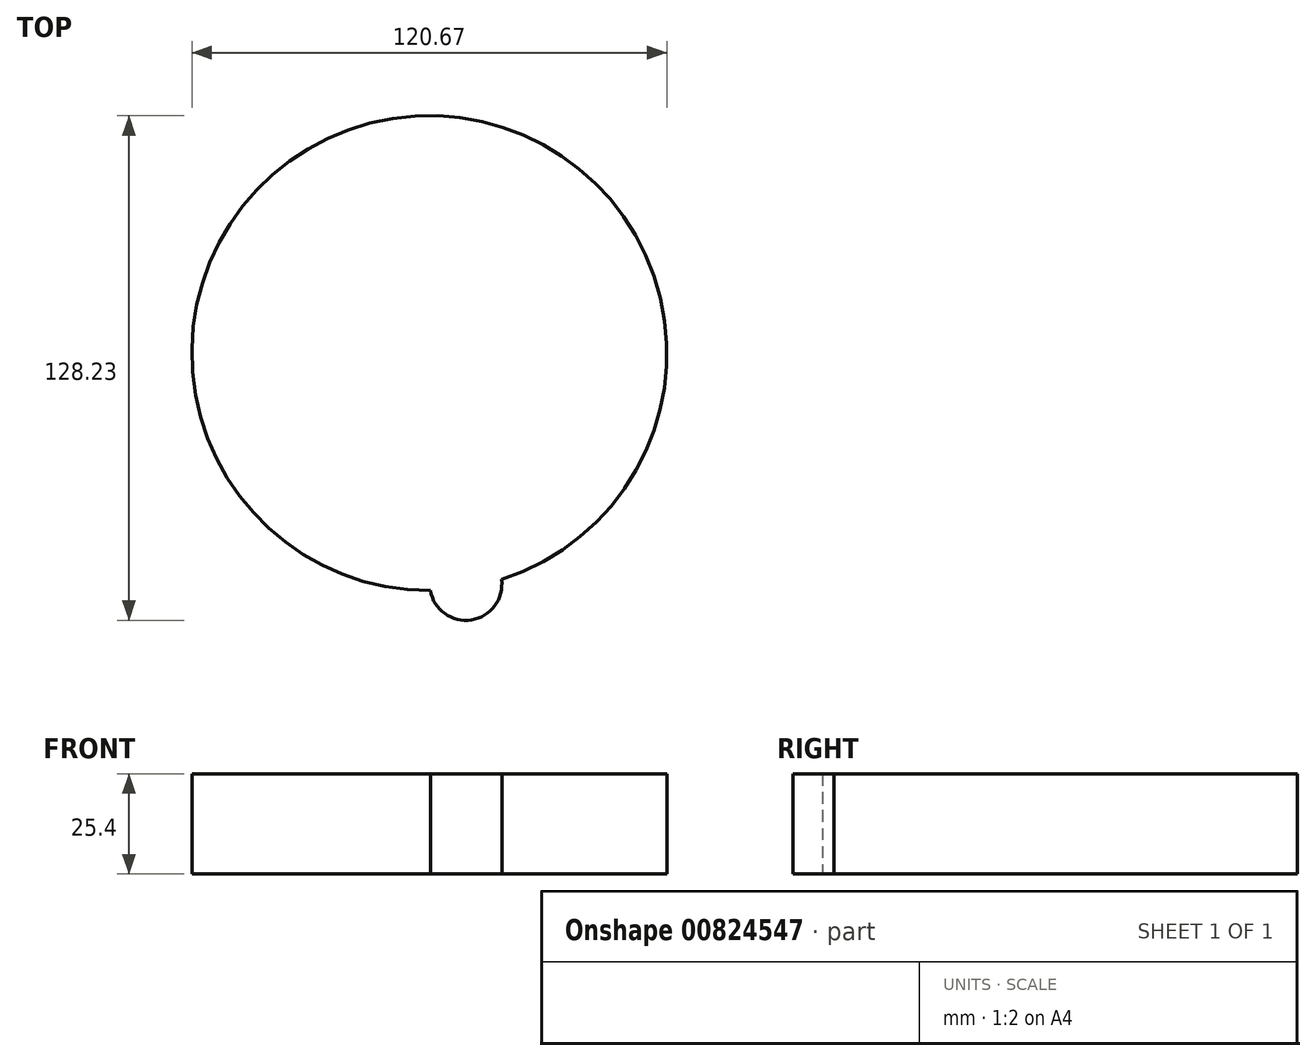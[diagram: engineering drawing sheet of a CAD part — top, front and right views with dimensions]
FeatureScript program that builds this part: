
annotation { "Feature Type Name" : "Feature", "Feature Type Description" : "" }
export const myFeature = defineFeature(function(context is Context, id is Id, definition is map)
    precondition{}
    {
        {
            var Q0;
            Q0=qCreatedBy(makeId("Top.planeOp"),FACE);
            var sketch = newSketch(context, id + "F0", { "sketchPlane" : qUnion([Q0])});
            skCircle(sketch, "E0", {"center": v(0, 0) * mm, "radius": 9.14 * mm});
            skCircle(sketch, "E1", {"center": v(-9.27, 58.75) * mm, "radius": 60.33 * mm});
            skSolve(sketch);
        }
        {
            var Q0;
            Q0 = qSketchRegion(id + "F0", true);
            extrude(context, id + "F1", {"entities" : qUnion([Q0]), "depth" : 25.4 * mm, "offsetDistance" : 25.4 * mm});
        }
    });
